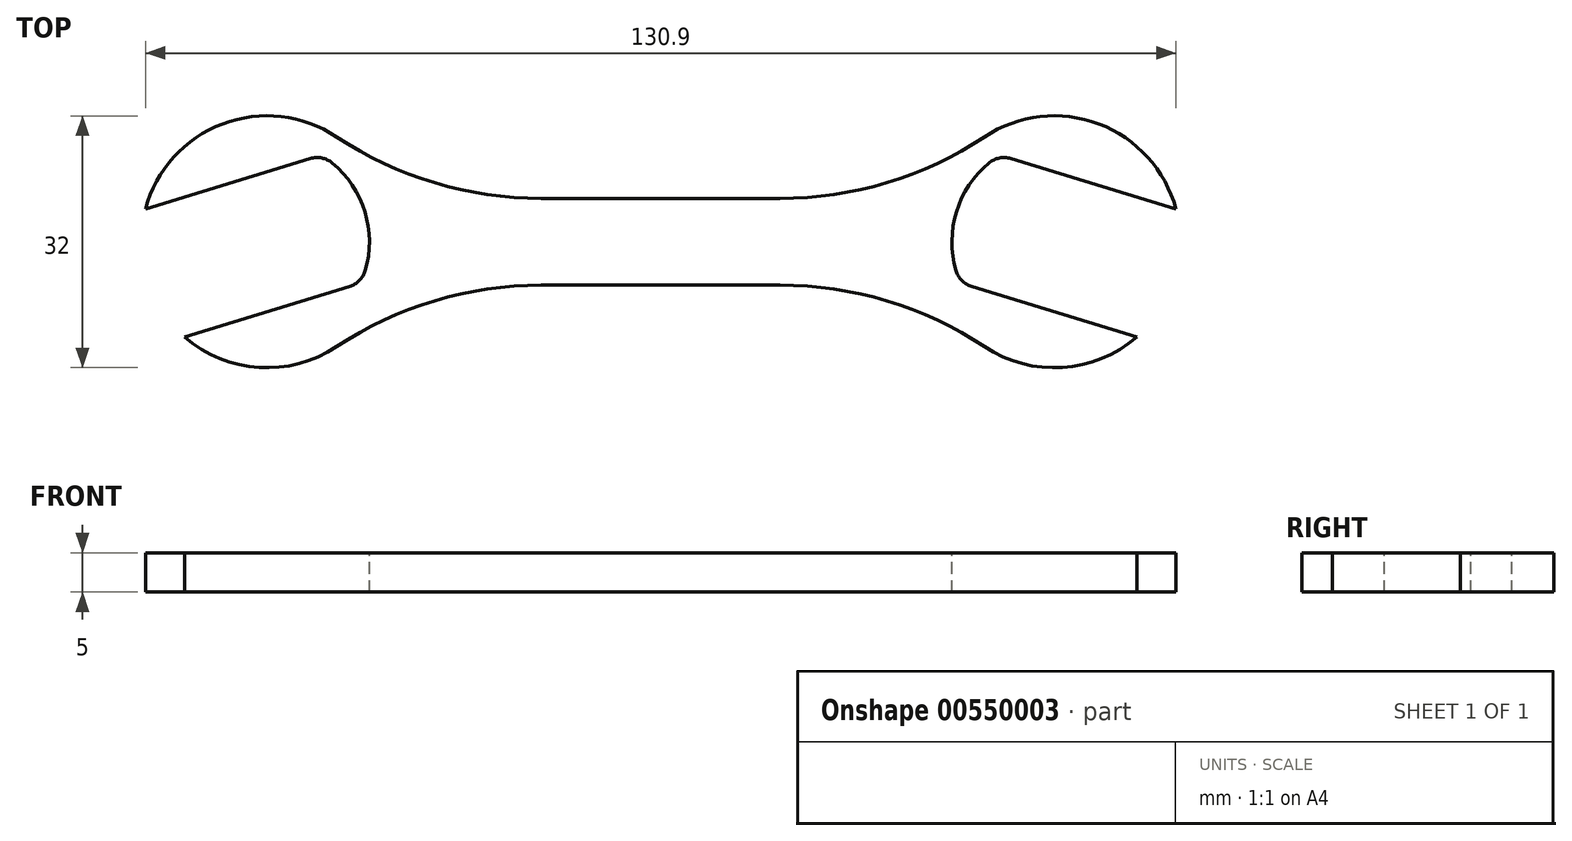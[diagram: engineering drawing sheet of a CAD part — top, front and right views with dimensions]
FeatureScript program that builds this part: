
annotation { "Feature Type Name" : "Feature", "Feature Type Description" : "" }
export const myFeature = defineFeature(function(context is Context, id is Id, definition is map)
    precondition{}
    {
        {
            var Q0;
            Q0=qCreatedBy(makeId("Top.planeOp"),FACE);
            var sketch = newSketch(context, id + "F0", { "sketchPlane" : qUnion([Q0])});
            skArc(sketch, "E0", {"start": v(-60.48, -12.1) * mm, "mid": v(-51.03, -15.97) * mm, "end": v(-41.16, -13.33) * mm});
            skLineSegment(sketch, "E1.0", {"start": v(-60.48, -12.1) * mm, "end": v(-38.1, -5.25) * mm});
            skArc(sketch, "E2", {"start": v(-38.1, -5.25) * mm, "mid": v(-37.57, 3.8) * mm, "end": v(-43.08, 11) * mm});
            skLineSegment(sketch, "E3", {"start": v(-65.45, 4.17) * mm, "end": v(-43.08, 11) * mm});
            skLineSegment(sketch, "E4", {"start": v(0, 5.5) * mm, "end": v(-15.18, 5.5) * mm});
            skLineSegment(sketch, "E5.MirrorCS", {"start": v(0, -5.5) * mm, "end": v(-15.18, -5.5) * mm});
            skArc(sketch, "E6.trimOffspring", {"start": v(-41.16, 13.33) * mm, "mid": v(-55.65, 14.97) * mm, "end": v(-65.45, 4.17) * mm});
            skPoint(sketch, "E7.visualSharp", {"position": v(-34.98, 5.5) * mm});
            skArc(sketch, "E7.filletArc", {"start": v(-41.16, 13.33) * mm, "mid": v(-28.74, 7.5) * mm, "end": v(-15.18, 5.5) * mm});
            skPoint(sketch, "E8.visualSharp", {"position": v(-34.98, -5.5) * mm});
            skArc(sketch, "E8.filletArc", {"start": v(-15.18, -5.5) * mm, "mid": v(-28.74, -7.5) * mm, "end": v(-41.16, -13.33) * mm});
            skArc(sketch, "E9.MirrorCS", {"start": v(41.16, 13.33) * mm, "mid": v(55.65, 14.97) * mm, "end": v(65.45, 4.17) * mm});
            skLineSegment(sketch, "E10.MirrorCS", {"start": v(65.45, 4.17) * mm, "end": v(43.08, 11) * mm});
            skArc(sketch, "E11.MirrorCS", {"start": v(38.1, -5.25) * mm, "mid": v(37.57, 3.8) * mm, "end": v(43.08, 11) * mm});
            skArc(sketch, "E12.MirrorCS", {"start": v(41.16, 13.33) * mm, "mid": v(28.74, 7.5) * mm, "end": v(15.18, 5.5) * mm});
            skLineSegment(sketch, "E13.MirrorCS", {"start": v(0, 5.5) * mm, "end": v(15.18, 5.5) * mm});
            skLineSegment(sketch, "E14.MirrorCS", {"start": v(0, -5.5) * mm, "end": v(15.18, -5.5) * mm});
            skArc(sketch, "E15.MirrorCS", {"start": v(15.18, -5.5) * mm, "mid": v(28.74, -7.5) * mm, "end": v(41.16, -13.33) * mm});
            skArc(sketch, "E16.MirrorCS", {"start": v(60.48, -12.1) * mm, "mid": v(51.03, -15.97) * mm, "end": v(41.16, -13.33) * mm});
            skLineSegment(sketch, "E17.MirrorCS", {"start": v(60.48, -12.1) * mm, "end": v(38.1, -5.25) * mm});
            skSolve(sketch);
        }
        {
            var Q0;
            Q0 = qSketchRegion(id + "F0", true);
            extrude(context, id + "F1", {"entities" : qUnion([Q0]), "oppositeDirection" : true, "depth" : 5 * mm, "offsetDistance" : 25 * mm});
        }
        {
            var Q0;
            Q0=makeQuery(id+"F1.opExtrude","SWEPT_EDGE",EDGE,{"disambiguationData":[OSD([sQuery(id+"F0.wireOp",EDGE,"E1.0"),sQuery(id+"F0.wireOp",EDGE,"E2")])]});
            var Q1;
            Q1=makeQuery(id+"F1.opExtrude","SWEPT_EDGE",EDGE,{"disambiguationData":[OSD([sQuery(id+"F0.wireOp",EDGE,"E2"),sQuery(id+"F0.wireOp",EDGE,"E3")])]});
            var Q2;
            Q2=makeQuery(id+"F1.opExtrude","SWEPT_EDGE",EDGE,{"disambiguationData":[OSD([sQuery(id+"F0.wireOp",EDGE,"E10.MirrorCS"),sQuery(id+"F0.wireOp",EDGE,"E11.MirrorCS")])]});
            var Q3;
            Q3=makeQuery(id+"F1.opExtrude","SWEPT_EDGE",EDGE,{"disambiguationData":[OSD([sQuery(id+"F0.wireOp",EDGE,"E11.MirrorCS"),sQuery(id+"F0.wireOp",EDGE,"E17.MirrorCS")])]});
            fillet(context, id + "F2", {"entities" : qUnion([Q0, Q1, Q2, Q3]), "radius" : 3 * mm, "tangentPropagation" : true, "allowEdgeOverflow" : false});
        }
    });
